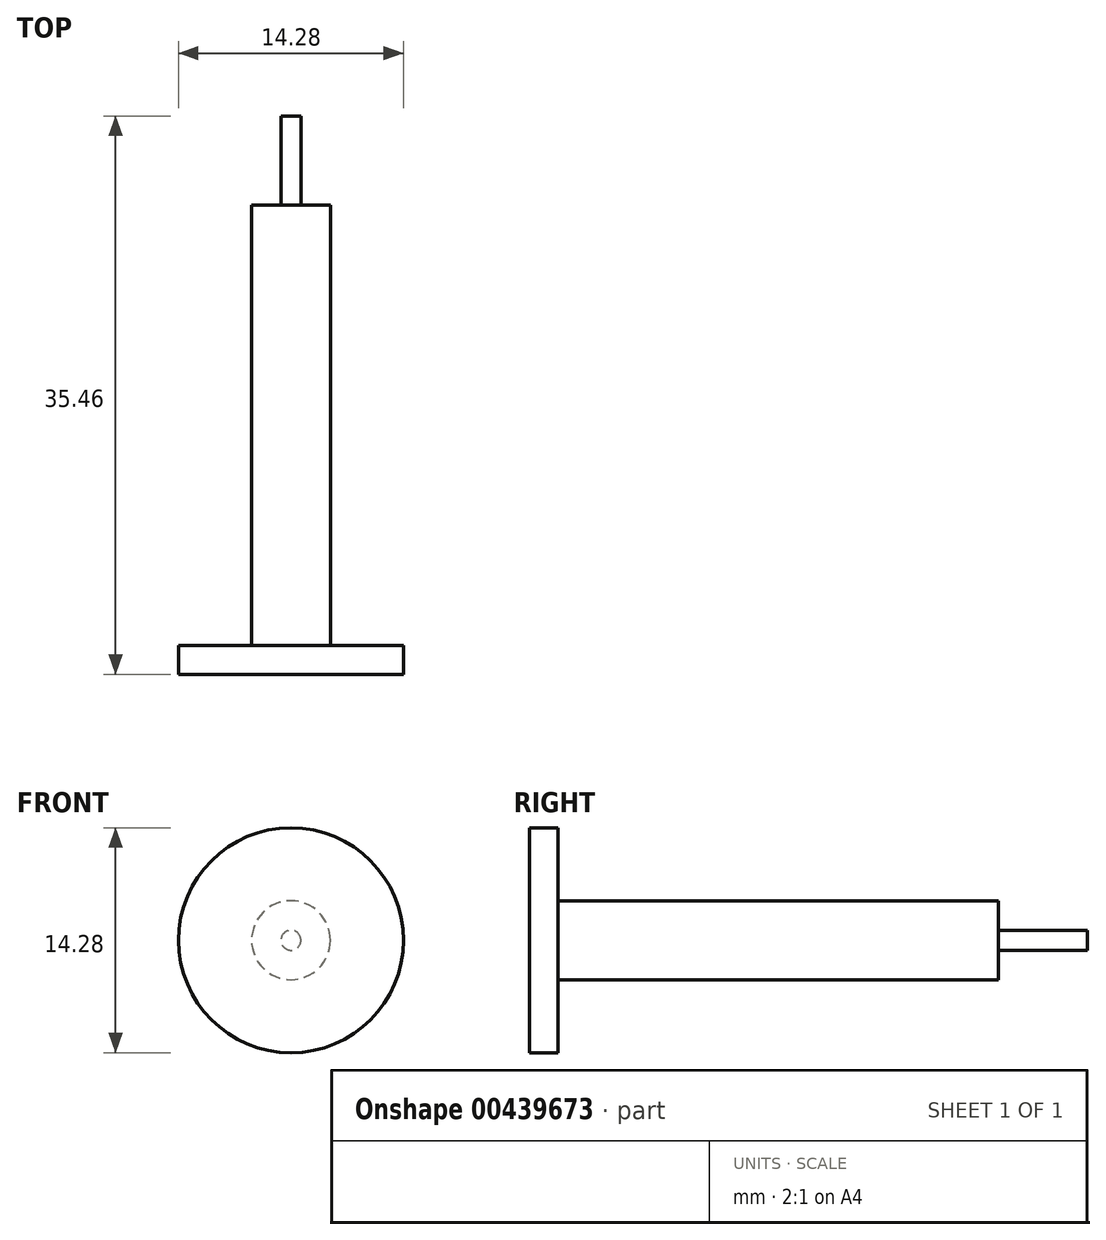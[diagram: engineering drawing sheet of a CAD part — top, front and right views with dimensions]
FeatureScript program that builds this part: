
annotation { "Feature Type Name" : "Feature", "Feature Type Description" : "" }
export const myFeature = defineFeature(function(context is Context, id is Id, definition is map)
    precondition{}
    {
        {
            var Q0;
            Q0=qCreatedBy(makeId("Right.planeOp"),FACE);
            var sketch = newSketch(context, id + "F0", { "sketchPlane" : qUnion([Q0])});
            skLineSegment(sketch, "E0", {"start": v(0, 0) * mm, "end": v(0, 7.14) * mm});
            skLineSegment(sketch, "E1", {"start": v(0, 7.14) * mm, "end": v(9.55, 7.14) * mm});
            skLineSegment(sketch, "E2", {"start": v(9.55, 7.14) * mm, "end": v(9.55, 2.5) * mm});
            skLineSegment(sketch, "E3", {"start": v(9.55, 2.5) * mm, "end": v(37.52, 2.5) * mm});
            skLineSegment(sketch, "E4", {"start": v(37.52, 2.5) * mm, "end": v(37.52, 0.64) * mm});
            skLineSegment(sketch, "E5", {"start": v(37.52, 0.64) * mm, "end": v(43.18, 0.64) * mm});
            skLineSegment(sketch, "E6", {"start": v(43.18, 0.64) * mm, "end": v(43.18, 0) * mm});
            skLineSegment(sketch, "E7", {"start": v(43.18, 0) * mm, "end": v(0, 0) * mm});
            skLineSegment(sketch, "E8", {"start": v(0, 0) * mm, "end": v(-2.27, 0) * mm, "construction": true});
            skSolve(sketch);
        }
        {
            var Q0;
            Q0 = qSketchRegion(id + "F0", true);
            var Q1;
            Q1=sQuery(id+"F0.wireOp",EDGE,"E8");
            revolve(context, id + "F1", {"surfaceOperationType" : NewSurfaceOperationType.NEW, "entities" : qUnion([Q0]), "axis" : qUnion([Q1]), "revolveType" : RevolveType.FULL});
        }
        {
            var Q0;
            Q0=makeQuery(id+"F1.opRevolve","SWEPT_FACE",FACE,{"disambiguationData":[OSD([sQuery(id+"F0.wireOp",EDGE,"E0")])]});
            var sketch = newSketch(context, id + "F2", { "sketchPlane" : qUnion([Q0])});
            skCircle(sketch, "E9", {"center": v(0, 0) * mm, "radius": 9.53 * mm});
            skSolve(sketch);
        }
        {
            var Q0;
            Q0 = qSketchRegion(id + "F2", true);
            extrude(context, id + "F3", {"entities" : qUnion([Q0]), "operationType" : NewBodyOperationType.REMOVE, "oppositeDirection" : true, "depth" : 7.72 * mm, "offsetDistance" : 25.4 * mm});
        }
    });
